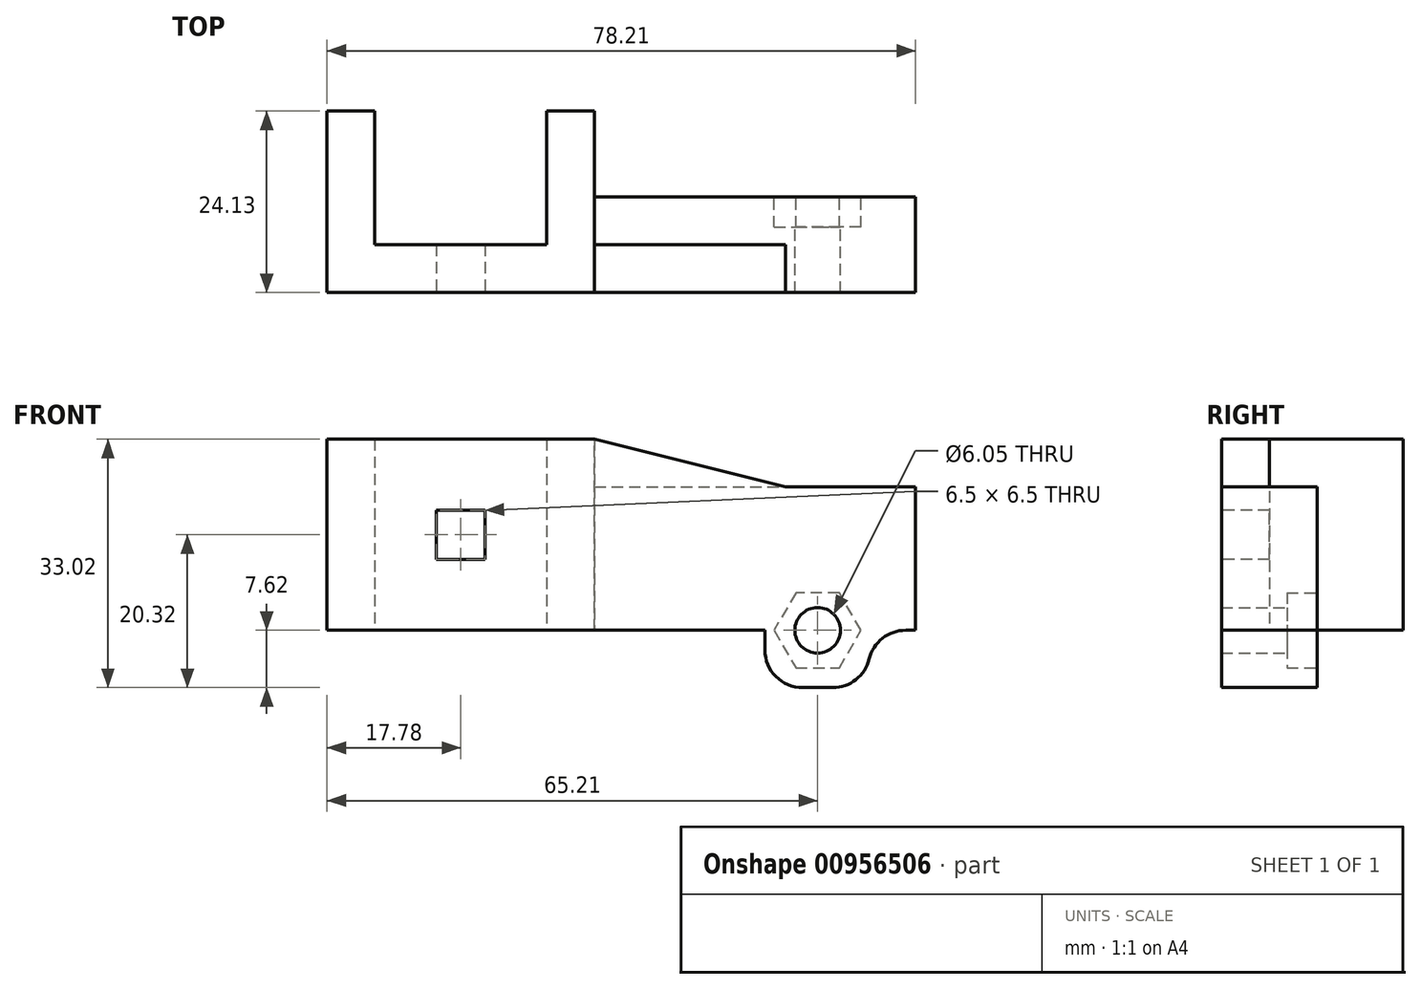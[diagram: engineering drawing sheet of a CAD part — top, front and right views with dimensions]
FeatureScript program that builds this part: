
annotation { "Feature Type Name" : "Feature", "Feature Type Description" : "" }
export const myFeature = defineFeature(function(context is Context, id is Id, definition is map)
    precondition{}
    {
        {
            var Q0;
            Q0=qCreatedBy(makeId("Top.planeOp"),FACE);
            var sketch = newSketch(context, id + "F0", { "sketchPlane" : qUnion([Q0])});
            skLineSegment(sketch, "E0.bottom", {"start": v(11.43, -9.78) * mm, "end": v(-11.43, -9.78) * mm});
            skLineSegment(sketch, "E0.top", {"start": v(11.43, 9.78) * mm, "end": v(4.83, 9.78) * mm});
            skLineSegment(sketch, "E0.left", {"start": v(11.43, -9.78) * mm, "end": v(11.43, 9.78) * mm});
            skLineSegment(sketch, "E0.right", {"start": v(-11.43, -9.78) * mm, "end": v(-11.43, 9.78) * mm});
            skPoint(sketch, "E0.middle", {"position": v(0, 0) * mm});
            skLineSegment(sketch, "E1.0", {"start": v(17.78, 16.13) * mm, "end": v(-17.78, 16.13) * mm});
            skLineSegment(sketch, "E1.1", {"start": v(17.78, -16.13) * mm, "end": v(17.78, 16.13) * mm});
            skLineSegment(sketch, "E1.2", {"start": v(17.78, -16.13) * mm, "end": v(-17.78, -16.13) * mm});
            skLineSegment(sketch, "E1.3", {"start": v(-17.78, -16.13) * mm, "end": v(-17.78, 16.13) * mm});
            skLineSegment(sketch, "E2.top", {"start": v(-7.37, 3.94) * mm, "end": v(4.83, 3.94) * mm});
            skLineSegment(sketch, "E2.left", {"start": v(-7.37, 9.78) * mm, "end": v(-7.37, 3.94) * mm});
            skLineSegment(sketch, "E2.right", {"start": v(4.83, 9.78) * mm, "end": v(4.83, 3.94) * mm});
            skLineSegment(sketch, "E3.trimOffspring", {"start": v(-7.37, 9.78) * mm, "end": v(-11.43, 9.78) * mm});
            skLineSegment(sketch, "E4", {"start": v(-17.78, 16.13) * mm, "end": v(-17.78, -16.13) * mm});
            skSolve(sketch);
        }
        {
            var Q0;
            Q0=makeQuery(id+"F0.imprint","IMPRINT",FACE,{"disambiguationData":[TD([[makeQuery(id+"F0.imprint","IMPRINT",EDGE,{"derivedFrom":sQuery(id+"F0.wireOp",EDGE,"E0.bottom")}),1.0]])]});
            extrude(context, id + "F1", {"entities" : qUnion([Q0]), "endBound" : BoundingType.SYMMETRIC, "depth" : 25.4 * mm, "offsetDistance" : 25.4 * mm});
        }
        {
            var Q0;
            Q0=makeQuery(id+"F1.opExtrude","SWEPT_FACE",FACE,{"disambiguationData":[OSD([sQuery(id+"F0.wireOp",EDGE,"E1.2")])]});
            var sketch = newSketch(context, id + "F2", { "sketchPlane" : qUnion([Q0])});
            skCircle(sketch, "E5", {"center": v(0, 0) * mm, "radius": 3.25 * mm});
            skSolve(sketch);
        }
        {
            var Q0;
            Q0=makeQuery(id+"F2.imprint","IMPRINT",FACE,{"disambiguationData":[TD([[makeQuery(id+"F2.imprint","IMPRINT",EDGE,{"derivedFrom":sQuery(id+"F2.wireOp",EDGE,"E5")}),1.0]])]});
            extrude(context, id + "F3", {"entities" : qUnion([Q0]), "operationType" : NewBodyOperationType.REMOVE, "endBound" : BoundingType.THROUGH_ALL, "oppositeDirection" : true, "depth" : 25.4 * mm, "offsetDistance" : 25.4 * mm});
        }
        {
            var Q0;
            Q0=makeQuery(id+"F1.opExtrude","SWEPT_FACE",FACE,{"disambiguationData":[OSD([sQuery(id+"F0.wireOp",EDGE,"E1.2")])]});
            var sketch = newSketch(context, id + "F4", { "sketchPlane" : qUnion([Q0])});
            skLineSegment(sketch, "E6.bottom", {"start": v(3.25, -3.25) * mm, "end": v(-3.25, -3.25) * mm});
            skLineSegment(sketch, "E6.top", {"start": v(3.25, 3.25) * mm, "end": v(-3.25, 3.25) * mm});
            skLineSegment(sketch, "E6.left", {"start": v(3.25, -3.25) * mm, "end": v(3.25, 3.25) * mm});
            skLineSegment(sketch, "E6.right", {"start": v(-3.25, -3.25) * mm, "end": v(-3.25, 3.25) * mm});
            skPoint(sketch, "E6.middle", {"position": v(0, 0) * mm});
            skSolve(sketch);
        }
        {
            var Q0;
            Q0=qSketchRegion(id+"F4",true);
            extrude(context, id + "F5", {"entities" : qUnion([Q0]), "operationType" : NewBodyOperationType.REMOVE, "oppositeDirection" : true, "depth" : 25.4 * mm, "offsetDistance" : 25.4 * mm});
        }
        {
            var Q0;
            Q0=makeQuery(id+"F1.opExtrude","CAP_FACE",FACE,{"disambiguationData":[OSD([sQuery(id+"F0.wireOp",EDGE,"E0.bottom"),sQuery(id+"F0.wireOp",EDGE,"E0.top"),sQuery(id+"F0.wireOp",EDGE,"E0.left"),sQuery(id+"F0.wireOp",EDGE,"E0.right"),sQuery(id+"F0.wireOp",EDGE,"E1.0"),sQuery(id+"F0.wireOp",EDGE,"E1.1"),sQuery(id+"F0.wireOp",EDGE,"E1.2"),sQuery(id+"F0.wireOp",EDGE,"E2.top"),sQuery(id+"F0.wireOp",EDGE,"E2.left"),sQuery(id+"F0.wireOp",EDGE,"E2.right"),sQuery(id+"F0.wireOp",EDGE,"E3.trimOffspring"),sQuery(id+"F0.wireOp",EDGE,"E4")])],"isStart":true});
            var sketch = newSketch(context, id + "F6", { "sketchPlane" : qUnion([Q0])});
            skLineSegment(sketch, "E7.bottom", {"start": v(17.78, 16.13) * mm, "end": v(60.43, 16.13) * mm});
            skLineSegment(sketch, "E7.top", {"start": v(17.78, 3.43) * mm, "end": v(60.43, 3.43) * mm});
            skLineSegment(sketch, "E7.left", {"start": v(17.78, 16.13) * mm, "end": v(17.78, 3.43) * mm});
            skLineSegment(sketch, "E7.right", {"start": v(60.43, 16.13) * mm, "end": v(60.43, 3.43) * mm});
            skSolve(sketch);
        }
        {
            var Q0;
            Q0=makeQuery(id+"F6.imprint","IMPRINT",FACE,{"disambiguationData":[TD([[makeQuery(id+"F6.imprint","IMPRINT",EDGE,{"derivedFrom":sQuery(id+"F6.wireOp",EDGE,"E7.bottom")}),-1.0]])]});
            extrude(context, id + "F7", {"entities" : qUnion([Q0]), "operationType" : NewBodyOperationType.ADD, "oppositeDirection" : true, "depth" : 19.05 * mm, "offsetDistance" : 25 * mm});
        }
        {
            var Q0;
            Q0=makeQuery(id+"F7.boolean.opBoolean","MERGE",FACE,{"derivedFrom":[makeQuery(id+"F1.opExtrude","SWEPT_FACE",FACE,{"disambiguationData":[OSD([sQuery(id+"F0.wireOp",EDGE,"E1.2")])]}),makeQuery(id+"F7.opExtrude","SWEPT_FACE",FACE,{"disambiguationData":[OSD([sQuery(id+"F6.wireOp",EDGE,"E7.bottom")])]})]});
            var sketch = newSketch(context, id + "F8", { "sketchPlane" : qUnion([Q0])});
            skLineSegment(sketch, "E8", {"start": v(17.78, 6.35) * mm, "end": v(43.18, 6.35) * mm});
            skLineSegment(sketch, "E9", {"start": v(43.18, 6.35) * mm, "end": v(17.78, 12.7) * mm});
            skLineSegment(sketch, "E10", {"start": v(17.78, 12.7) * mm, "end": v(17.78, 6.35) * mm});
            skSolve(sketch);
        }
        {
            var Q0;
            Q0=makeQuery(id+"F8.imprint","IMPRINT",FACE,{"disambiguationData":[TD([[makeQuery(id+"F8.imprint","IMPRINT",EDGE,{"derivedFrom":sQuery(id+"F8.wireOp",EDGE,"E8")}),1.0]])]});
            extrude(context, id + "F9", {"entities" : qUnion([Q0]), "operationType" : NewBodyOperationType.ADD, "oppositeDirection" : true, "depth" : 6.35 * mm, "offsetDistance" : 25 * mm});
        }
        {
            var Q0;
            Q0=makeQuery(id+"F7.boolean.opBoolean","MERGE",FACE,{"derivedFrom":[makeQuery(id+"F1.opExtrude","CAP_FACE",FACE,{"disambiguationData":[OSD([sQuery(id+"F0.wireOp",EDGE,"E0.bottom"),sQuery(id+"F0.wireOp",EDGE,"E0.top"),sQuery(id+"F0.wireOp",EDGE,"E0.left"),sQuery(id+"F0.wireOp",EDGE,"E0.right"),sQuery(id+"F0.wireOp",EDGE,"E1.0"),sQuery(id+"F0.wireOp",EDGE,"E1.1"),sQuery(id+"F0.wireOp",EDGE,"E1.2"),sQuery(id+"F0.wireOp",EDGE,"E2.top"),sQuery(id+"F0.wireOp",EDGE,"E2.left"),sQuery(id+"F0.wireOp",EDGE,"E2.right"),sQuery(id+"F0.wireOp",EDGE,"E3.trimOffspring"),sQuery(id+"F0.wireOp",EDGE,"E4")])],"isStart":true}),makeQuery(id+"F7.opExtrude","CAP_FACE",FACE,{"disambiguationData":[OSD([sQuery(id+"F6.wireOp",EDGE,"E7.bottom"),sQuery(id+"F6.wireOp",EDGE,"E7.top"),sQuery(id+"F6.wireOp",EDGE,"E7.left"),sQuery(id+"F6.wireOp",EDGE,"E7.right")])],"isStart":true})]});
            var sketch = newSketch(context, id + "F10", { "sketchPlane" : qUnion([Q0])});
            skLineSegment(sketch, "E11.bottom", {"start": v(54.43, 3.43) * mm, "end": v(40.43, 3.43) * mm});
            skLineSegment(sketch, "E11.top", {"start": v(54.43, 16.13) * mm, "end": v(40.43, 16.13) * mm});
            skLineSegment(sketch, "E11.left", {"start": v(54.43, 3.43) * mm, "end": v(54.43, 16.13) * mm});
            skLineSegment(sketch, "E11.right", {"start": v(40.43, 3.43) * mm, "end": v(40.43, 16.13) * mm});
            skPoint(sketch, "E11.middle", {"position": v(47.43, 9.78) * mm});
            skSolve(sketch);
        }
        {
            var Q0;
            Q0=qSketchRegion(id+"F10",true);
            extrude(context, id + "F11", {"entities" : qUnion([Q0]), "operationType" : NewBodyOperationType.ADD, "depth" : 7.62 * mm, "offsetDistance" : 25 * mm});
        }
        {
            var Q0;
            Q0=makeQuery(id+"F11.opExtrude","CAP_EDGE",EDGE,{"disambiguationData":[OSD([sQuery(id+"F10.wireOp",EDGE,"E11.right")])],"isStart":false});
            var Q1;
            Q1=makeQuery(id+"F11.opExtrude","CAP_EDGE",EDGE,{"disambiguationData":[OSD([sQuery(id+"F10.wireOp",EDGE,"E11.left")])],"isStart":false});
            fillet(context, id + "F12", {"entities" : qUnion([Q0, Q1]), "radius" : 5 * mm, "tangentPropagation" : true, "allowEdgeOverflow" : false});
        }
        {
            var Q0;
            Q0=makeQuery(id+"F11.boolean.opBoolean","MERGE",FACE,{"derivedFrom":[makeQuery(id+"F7.opExtrude","SWEPT_FACE",FACE,{"disambiguationData":[OSD([sQuery(id+"F6.wireOp",EDGE,"E7.top")])]}),makeQuery(id+"F11.opExtrude","SWEPT_FACE",FACE,{"disambiguationData":[OSD([sQuery(id+"F10.wireOp",EDGE,"E11.bottom")])]})]});
            var sketch = newSketch(context, id + "F13", { "sketchPlane" : qUnion([Q0])});
            skCircle(sketch, "E12", {"center": v(-47.43, -12.7) * mm, "radius": 3.02 * mm});
            skPoint(sketch, "E12.centerSnap0", {"position": v(-47.43, -20.32) * mm});
            skSolve(sketch);
        }
        {
            var Q0;
            Q0=makeQuery(id+"F13.imprint","IMPRINT",FACE,{"disambiguationData":[TD([[makeQuery(id+"F13.imprint","IMPRINT",EDGE,{"derivedFrom":sQuery(id+"F13.wireOp",EDGE,"E12")}),1.0]])]});
            extrude(context, id + "F14", {"entities" : qUnion([Q0]), "operationType" : NewBodyOperationType.REMOVE, "endBound" : BoundingType.THROUGH_ALL, "oppositeDirection" : true, "depth" : 25 * mm, "offsetDistance" : 25 * mm});
        }
        {
            var Q0;
            Q0=makeQuery(id+"F11.boolean.opBoolean","MERGE",FACE,{"derivedFrom":[makeQuery(id+"F7.opExtrude","SWEPT_FACE",FACE,{"disambiguationData":[OSD([sQuery(id+"F6.wireOp",EDGE,"E7.top")])]}),makeQuery(id+"F11.opExtrude","SWEPT_FACE",FACE,{"disambiguationData":[OSD([sQuery(id+"F10.wireOp",EDGE,"E11.bottom")])]})]});
            var sketch = newSketch(context, id + "F15", { "sketchPlane" : qUnion([Q0])});
            skCircle(sketch, "E13.cCircle", {"center": v(-47.43, -12.7) * mm, "radius": 5 * mm, "construction": true});
            skLineSegment(sketch, "E13.0", {"start": v(-44.54, -17.7) * mm, "end": v(-50.32, -17.7) * mm});
            skLineSegment(sketch, "E13.1", {"start": v(-50.32, -17.7) * mm, "end": v(-53.2, -12.7) * mm});
            skLineSegment(sketch, "E13.2", {"start": v(-53.2, -12.7) * mm, "end": v(-50.32, -7.7) * mm});
            skLineSegment(sketch, "E13.3", {"start": v(-50.32, -7.7) * mm, "end": v(-44.54, -7.7) * mm});
            skLineSegment(sketch, "E13.4", {"start": v(-44.54, -7.7) * mm, "end": v(-41.66, -12.7) * mm});
            skLineSegment(sketch, "E13.5", {"start": v(-41.66, -12.7) * mm, "end": v(-44.54, -17.7) * mm});
            skPoint(sketch, "E13.0.midPoint", {"position": v(-47.43, -17.7) * mm});
            skSolve(sketch);
        }
        {
            var Q0;
            Q0=makeQuery(id+"F15.imprint","IMPRINT",FACE,{"disambiguationData":[TD([[makeQuery(id+"F15.imprint","IMPRINT",EDGE,{"derivedFrom":sQuery(id+"F15.wireOp",EDGE,"E13.0")}),-1.0]])]});
            extrude(context, id + "F16", {"entities" : qUnion([Q0]), "operationType" : NewBodyOperationType.REMOVE, "oppositeDirection" : true, "depth" : 4 * mm, "offsetDistance" : 25 * mm});
        }
        {
            var Q0;
            Q0=makeQuery(id+"F11.opExtrude","CAP_EDGE",EDGE,{"disambiguationData":[OSD([sQuery(id+"F10.wireOp",EDGE,"E11.left")])],"isStart":true});
            var Q1;
            Q1=makeQuery(id+"F11.opExtrude","CAP_EDGE",EDGE,{"disambiguationData":[OSD([sQuery(id+"F10.wireOp",EDGE,"E11.right")])],"isStart":true});
            fillet(context, id + "F17", {"entities" : qUnion([Q0, Q1]), "radius" : 5 * mm, "tangentPropagation" : true, "allowEdgeOverflow" : false});
        }
        {
            var Q0;
            Q0=makeQuery(id+"F1.opExtrude","CAP_FACE",FACE,{"disambiguationData":[OSD([sQuery(id+"F0.wireOp",EDGE,"E0.bottom"),sQuery(id+"F0.wireOp",EDGE,"E0.top"),sQuery(id+"F0.wireOp",EDGE,"E0.left"),sQuery(id+"F0.wireOp",EDGE,"E0.right"),sQuery(id+"F0.wireOp",EDGE,"E1.0"),sQuery(id+"F0.wireOp",EDGE,"E1.1"),sQuery(id+"F0.wireOp",EDGE,"E1.2"),sQuery(id+"F0.wireOp",EDGE,"E2.top"),sQuery(id+"F0.wireOp",EDGE,"E2.left"),sQuery(id+"F0.wireOp",EDGE,"E2.right"),sQuery(id+"F0.wireOp",EDGE,"E3.trimOffspring"),sQuery(id+"F0.wireOp",EDGE,"E4")])],"isStart":false});
            var sketch = newSketch(context, id + "F18", { "sketchPlane" : qUnion([Q0])});
            skLineSegment(sketch, "E14.bottom", {"start": v(-17.78, -16.13) * mm, "end": v(17.78, -16.13) * mm});
            skLineSegment(sketch, "E14.top", {"start": v(-17.78, 8) * mm, "end": v(17.78, 8) * mm});
            skLineSegment(sketch, "E14.left", {"start": v(-17.78, -16.13) * mm, "end": v(-17.78, 8) * mm});
            skLineSegment(sketch, "E14.right", {"start": v(17.78, -16.13) * mm, "end": v(17.78, 8) * mm});
            skLineSegment(sketch, "E15.bottom", {"start": v(-17.78, 16.13) * mm, "end": v(17.78, 16.13) * mm});
            skLineSegment(sketch, "E15.left", {"start": v(-17.78, 16.13) * mm, "end": v(-17.78, 8) * mm});
            skLineSegment(sketch, "E15.right", {"start": v(17.78, 16.13) * mm, "end": v(17.78, 8) * mm});
            skSolve(sketch);
        }
        {
            var Q0;
            Q0=makeQuery(id+"F18.imprint","IMPRINT",FACE,{"disambiguationData":[TD([[makeQuery(id+"F18.imprint","IMPRINT",EDGE,{"derivedFrom":sQuery(id+"F18.wireOp",EDGE,"E15.bottom")}),1.0]])]});
            extrude(context, id + "F19", {"entities" : qUnion([Q0]), "operationType" : NewBodyOperationType.REMOVE, "oppositeDirection" : true, "depth" : 50.8 * mm, "offsetDistance" : 25 * mm});
        }
        {
            var Q0;
            {var subQ0=sQuery(id+"F0.wireOp",EDGE,"E2.top");var subQ1=sQuery(id+"F0.wireOp",EDGE,"E2.left");var subQ2=sQuery(id+"F0.wireOp",EDGE,"E2.right");Q0=makeQuery(id+"F19.boolean.opBoolean","SPLIT",FACE,{"disambiguationData":[TD([makeQuery(id+"F1.opExtrude","SWEPT_FACE",FACE,{"disambiguationData":[OSD([subQ0])]})])],"derivedFrom":makeQuery(id+"F1.opExtrude","CAP_FACE",FACE,{"disambiguationData":[OSD([sQuery(id+"F0.wireOp",EDGE,"E0.bottom"),sQuery(id+"F0.wireOp",EDGE,"E0.top"),sQuery(id+"F0.wireOp",EDGE,"E0.left"),sQuery(id+"F0.wireOp",EDGE,"E0.right"),sQuery(id+"F0.wireOp",EDGE,"E1.0"),sQuery(id+"F0.wireOp",EDGE,"E1.1"),sQuery(id+"F0.wireOp",EDGE,"E1.2"),subQ0,subQ1,subQ2,sQuery(id+"F0.wireOp",EDGE,"E3.trimOffspring"),sQuery(id+"F0.wireOp",EDGE,"E4")])],"isStart":false})});}
            var sketch = newSketch(context, id + "F20", { "sketchPlane" : qUnion([Q0])});
            skLineSegment(sketch, "E16.bottom", {"start": v(7.98, 1.54) * mm, "end": v(-7.98, 1.54) * mm});
            skLineSegment(sketch, "E16.top", {"start": v(7.98, 11.17) * mm, "end": v(-7.98, 11.17) * mm});
            skLineSegment(sketch, "E16.left", {"start": v(7.98, 1.54) * mm, "end": v(7.98, 11.17) * mm});
            skLineSegment(sketch, "E16.right", {"start": v(-7.98, 1.54) * mm, "end": v(-7.98, 11.17) * mm});
            skPoint(sketch, "E16.middle", {"position": v(0, 6.35) * mm});
            skSolve(sketch);
        }
        {
            var Q0;
            Q0=qSketchRegion(id+"F20",true);
            extrude(context, id + "F21", {"entities" : qUnion([Q0]), "operationType" : NewBodyOperationType.REMOVE, "oppositeDirection" : true, "depth" : 50.8 * mm, "offsetDistance" : 25 * mm});
        }
    });
